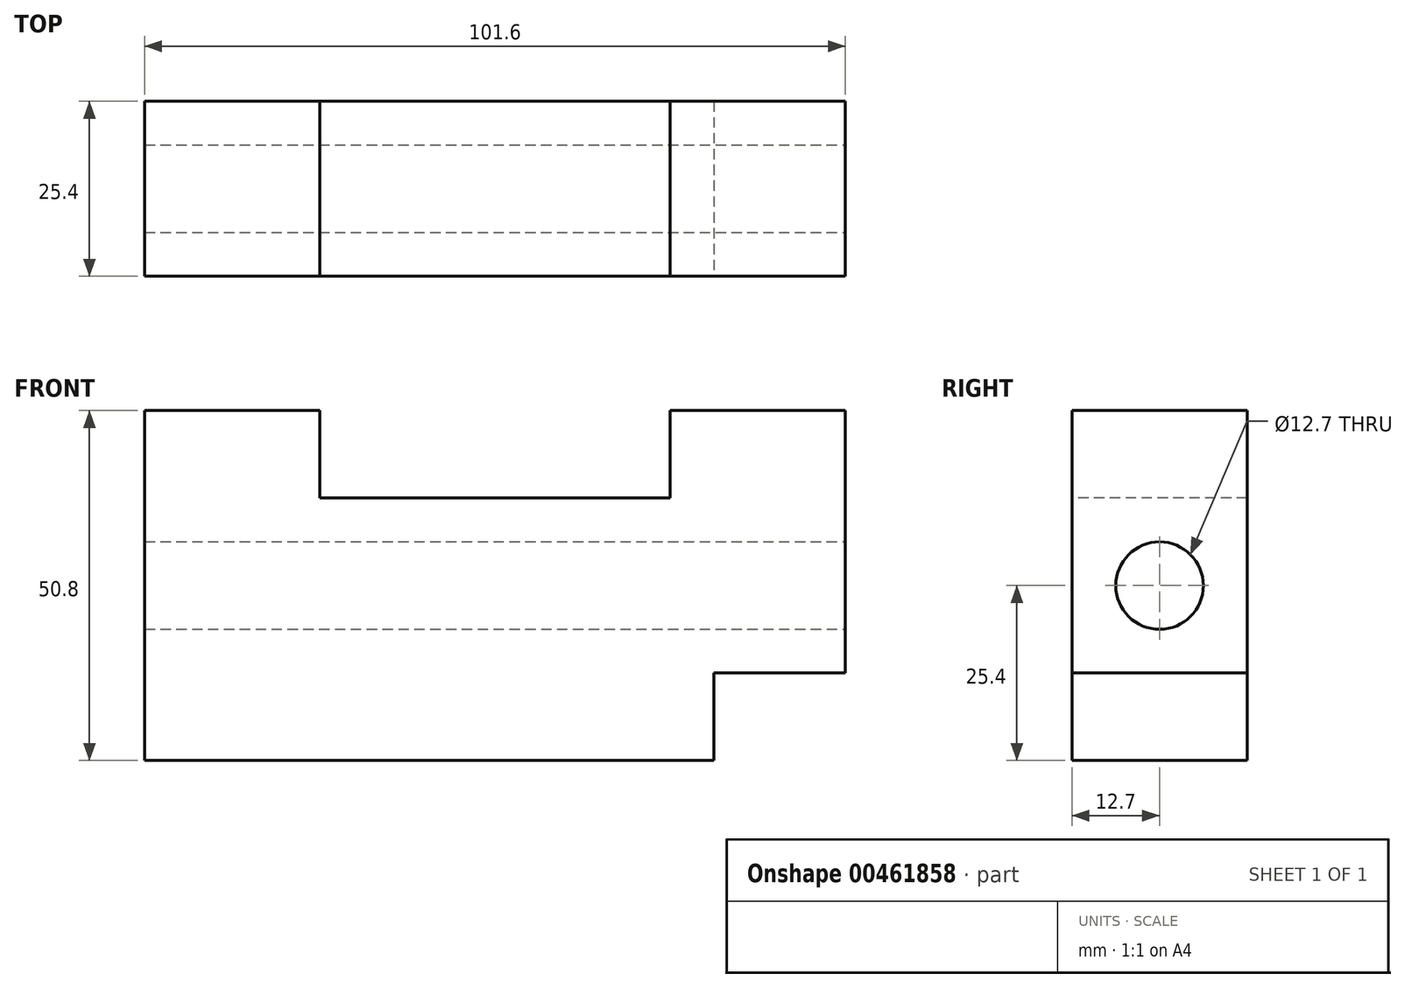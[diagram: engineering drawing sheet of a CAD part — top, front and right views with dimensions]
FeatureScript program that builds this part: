
annotation { "Feature Type Name" : "Feature", "Feature Type Description" : "" }
export const myFeature = defineFeature(function(context is Context, id is Id, definition is map)
    precondition{}
    {
        {
            var Q0;
            Q0=qCreatedBy(makeId("Front.planeOp"),FACE);
            var sketch = newSketch(context, id + "F0", { "sketchPlane" : qUnion([Q0])});
            skLineSegment(sketch, "E0.bottom", {"start": v(-50.8, 25.4) * mm, "end": v(50.8, 25.4) * mm});
            skLineSegment(sketch, "E0.top", {"start": v(-50.8, -25.4) * mm, "end": v(50.8, -25.4) * mm});
            skLineSegment(sketch, "E0.left", {"start": v(-50.8, 25.4) * mm, "end": v(-50.8, -25.4) * mm});
            skLineSegment(sketch, "E0.right", {"start": v(50.8, 25.4) * mm, "end": v(50.8, -25.4) * mm});
            skPoint(sketch, "E0.middle", {"position": v(0, 0) * mm});
            skSolve(sketch);
        }
        {
            var Q0;
            Q0 = qSketchRegion(id + "F0", true);
            extrude(context, id + "F1", {"entities" : qUnion([Q0]), "depth" : 25.4 * mm});
        }
        {
            var Q0;
            Q0=makeQuery(id+"F1.opExtrude","CAP_FACE",FACE,{"disambiguationData":[OSD([sQuery(id+"F0.wireOp",EDGE,"E0.bottom"),sQuery(id+"F0.wireOp",EDGE,"E0.top"),sQuery(id+"F0.wireOp",EDGE,"E0.left"),sQuery(id+"F0.wireOp",EDGE,"E0.right")])],"isStart":false});
            var sketch = newSketch(context, id + "F2", { "sketchPlane" : qUnion([Q0])});
            skLineSegment(sketch, "E1.bottom", {"start": v(-25.4, 25.4) * mm, "end": v(25.4, 25.4) * mm});
            skLineSegment(sketch, "E1.top", {"start": v(-25.4, 12.7) * mm, "end": v(25.4, 12.7) * mm});
            skLineSegment(sketch, "E1.left", {"start": v(-25.4, 25.4) * mm, "end": v(-25.4, 12.7) * mm});
            skLineSegment(sketch, "E1.right", {"start": v(25.4, 25.4) * mm, "end": v(25.4, 12.7) * mm});
            skSolve(sketch);
        }
        {
            var Q0;
            Q0 = qSketchRegion(id + "F2", true);
            extrude(context, id + "F3", {"entities" : qUnion([Q0]), "operationType" : NewBodyOperationType.REMOVE, "oppositeDirection" : true, "depth" : 25.4 * mm});
        }
        {
            var Q0;
            Q0=makeQuery(id+"F1.opExtrude","CAP_FACE",FACE,{"disambiguationData":[OSD([sQuery(id+"F0.wireOp",EDGE,"E0.bottom"),sQuery(id+"F0.wireOp",EDGE,"E0.top"),sQuery(id+"F0.wireOp",EDGE,"E0.left"),sQuery(id+"F0.wireOp",EDGE,"E0.right")])],"isStart":false});
            var sketch = newSketch(context, id + "F4", { "sketchPlane" : qUnion([Q0])});
            skLineSegment(sketch, "E2.bottom", {"start": v(50.8, -12.7) * mm, "end": v(31.75, -12.7) * mm});
            skLineSegment(sketch, "E2.top", {"start": v(50.8, -25.4) * mm, "end": v(31.75, -25.4) * mm});
            skLineSegment(sketch, "E2.left", {"start": v(50.8, -12.7) * mm, "end": v(50.8, -25.4) * mm});
            skLineSegment(sketch, "E2.right", {"start": v(31.75, -12.7) * mm, "end": v(31.75, -25.4) * mm});
            skSolve(sketch);
        }
        {
            var Q0;
            Q0 = qSketchRegion(id + "F4", true);
            extrude(context, id + "F5", {"entities" : qUnion([Q0]), "operationType" : NewBodyOperationType.REMOVE, "oppositeDirection" : true, "depth" : 25.4 * mm});
        }
        {
            var Q0;
            Q0=makeQuery(id+"F1.opExtrude","SWEPT_FACE",FACE,{"disambiguationData":[OSD([sQuery(id+"F0.wireOp",EDGE,"E0.right")])]});
            var sketch = newSketch(context, id + "F6", { "sketchPlane" : qUnion([Q0])});
            skCircle(sketch, "E3", {"center": v(-12.7, 0) * mm, "radius": 6.35 * mm});
            skSolve(sketch);
        }
        {
            var Q0;
            Q0=makeQuery(id+"F6.imprint","IMPRINT",FACE,{"disambiguationData":[TD([[makeQuery(id+"F6.imprint","IMPRINT",EDGE,{"derivedFrom":sQuery(id+"F6.wireOp",EDGE,"E3")}),1.0]])]});
            extrude(context, id + "F7", {"entities" : qUnion([Q0]), "operationType" : NewBodyOperationType.REMOVE, "oppositeDirection" : true, "depth" : 101.6 * mm});
        }
    });
